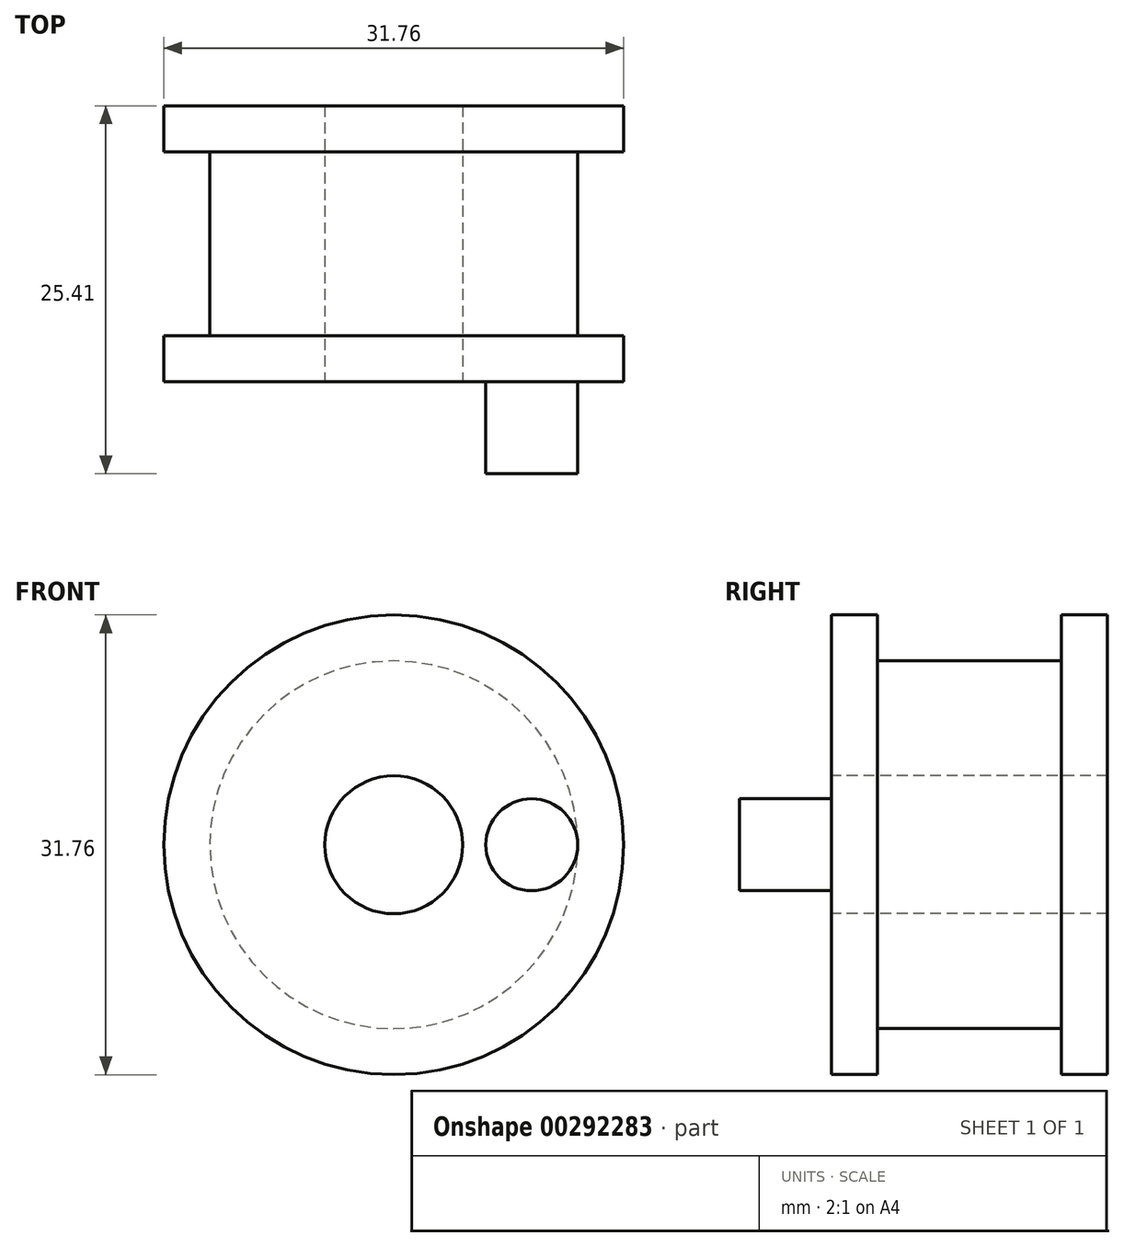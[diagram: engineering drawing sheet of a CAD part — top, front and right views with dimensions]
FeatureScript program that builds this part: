
annotation { "Feature Type Name" : "Feature", "Feature Type Description" : "" }
export const myFeature = defineFeature(function(context is Context, id is Id, definition is map)
    precondition{}
    {
        {
            var Q0;
            Q0=qCreatedBy(makeId("Front.planeOp"),FACE);
            var sketch = newSketch(context, id + "F0", { "sketchPlane" : qUnion([Q0])});
            skCircle(sketch, "E0", {"center": v(0, 0) * mm, "radius": 12.7 * mm});
            skSolve(sketch);
        }
        {
            var Q0;
            Q0=makeQuery(id+"F0.imprint","IMPRINT",FACE,{"disambiguationData":[TD([[makeQuery(id+"F0.imprint","IMPRINT",EDGE,{"derivedFrom":sQuery(id+"F0.wireOp",EDGE,"E0")}),1.0]])]});
            extrude(context, id + "F1", {"entities" : qUnion([Q0]), "depth" : 12.7 * mm});
        }
        {
            var Q0;
            Q0=makeQuery(id+"F1.opExtrude","CAP_FACE",FACE,{"disambiguationData":[OSD([sQuery(id+"F0.wireOp",EDGE,"E0")])],"isStart":false});
            var sketch = newSketch(context, id + "F2", { "sketchPlane" : qUnion([Q0])});
            skCircle(sketch, "E1", {"center": v(0, 0) * mm, "radius": 15.88 * mm});
            skSolve(sketch);
        }
        {
            var Q0;
            Q0=makeQuery(id+"F2.imprint","IMPRINT",FACE,{"disambiguationData":[TD([[makeQuery(id+"F2.imprint","IMPRINT",EDGE,{"derivedFrom":sQuery(id+"F2.wireOp",EDGE,"E1")}),1.0]])]});
            var Q1;
            Q1=makeQuery(id+"F2.imprint","IMPRINT",FACE,{"disambiguationData":[TD([[makeQuery(id+"F2.imprint","IMPRINT",EDGE,{"derivedFrom":makeQuery(id+"F1.opExtrude","CAP_EDGE",EDGE,{"disambiguationData":[OSD([sQuery(id+"F0.wireOp",EDGE,"E0")])],"isStart":false})}),1.0]])]});
            extrude(context, id + "F3", {"entities" : qUnion([Q0, Q1]), "operationType" : NewBodyOperationType.ADD, "depth" : 3.17 * mm});
        }
        {
            var Q0;
            Q0=makeQuery(id+"F1.opExtrude","CAP_FACE",FACE,{"disambiguationData":[OSD([sQuery(id+"F0.wireOp",EDGE,"E0")])],"isStart":true});
            var sketch = newSketch(context, id + "F4", { "sketchPlane" : qUnion([Q0])});
            skCircle(sketch, "E2", {"center": v(0, 0) * mm, "radius": 15.88 * mm});
            skSolve(sketch);
        }
        {
            var Q0;
            Q0=makeQuery(id+"F4.imprint","IMPRINT",FACE,{"disambiguationData":[TD([[makeQuery(id+"F4.imprint","IMPRINT",EDGE,{"derivedFrom":sQuery(id+"F4.wireOp",EDGE,"E2")}),1.0]])]});
            var Q1;
            Q1=makeQuery(id+"F4.imprint","IMPRINT",FACE,{"disambiguationData":[TD([[makeQuery(id+"F4.imprint","IMPRINT",EDGE,{"derivedFrom":makeQuery(id+"F1.opExtrude","CAP_EDGE",EDGE,{"disambiguationData":[OSD([sQuery(id+"F0.wireOp",EDGE,"E0")])],"isStart":true})}),-1.0]])]});
            extrude(context, id + "F5", {"entities" : qUnion([Q0, Q1]), "operationType" : NewBodyOperationType.ADD, "depth" : 3.17 * mm});
        }
        {
            var Q0;
            Q0=makeQuery(id+"F3.opExtrude","CAP_FACE",FACE,{"disambiguationData":[OSD([sQuery(id+"F2.wireOp",EDGE,"E1")])],"isStart":false});
            var sketch = newSketch(context, id + "F6", { "sketchPlane" : qUnion([Q0])});
            skCircle(sketch, "E3", {"center": v(0, 0) * mm, "radius": 4.76 * mm});
            skLineSegment(sketch, "E4", {"start": v(0, 0) * mm, "end": v(9.53, 0) * mm});
            skCircle(sketch, "E5", {"center": v(9.53, 0) * mm, "radius": 3.18 * mm});
            skSolve(sketch);
        }
        {
            var Q0;
            Q0=makeQuery(id+"F6.imprint","IMPRINT",FACE,{"disambiguationData":[TD([[makeQuery(id+"F6.imprint","IMPRINT",EDGE,{"derivedFrom":sQuery(id+"F6.wireOp",EDGE,"E5")}),1.0]])]});
            extrude(context, id + "F7", {"entities" : qUnion([Q0]), "operationType" : NewBodyOperationType.ADD, "depth" : 6.35 * mm});
        }
        {
            var Q0;
            Q0=makeQuery(id+"F3.opExtrude","CAP_FACE",FACE,{"disambiguationData":[OSD([sQuery(id+"F2.wireOp",EDGE,"E1")])],"isStart":false});
            var sketch = newSketch(context, id + "F8", { "sketchPlane" : qUnion([Q0])});
            skCircle(sketch, "E6", {"center": v(0, 0) * mm, "radius": 4.76 * mm});
            skSolve(sketch);
        }
        {
            var Q0;
            Q0=makeQuery(id+"F8.imprint","IMPRINT",FACE,{"disambiguationData":[TD([[makeQuery(id+"F8.imprint","IMPRINT",EDGE,{"derivedFrom":sQuery(id+"F8.wireOp",EDGE,"E6")}),1.0]])]});
            var Q1;
            Q1=sQuery(id+"F8.wireOp",EDGE,"E6");
            extrude(context, id + "F9", {"entities" : qUnion([Q0]), "operationType" : NewBodyOperationType.REMOVE, "surfaceEntities" : qUnion([Q1]), "oppositeDirection" : true, "depth" : 50.8 * mm});
        }
    });
